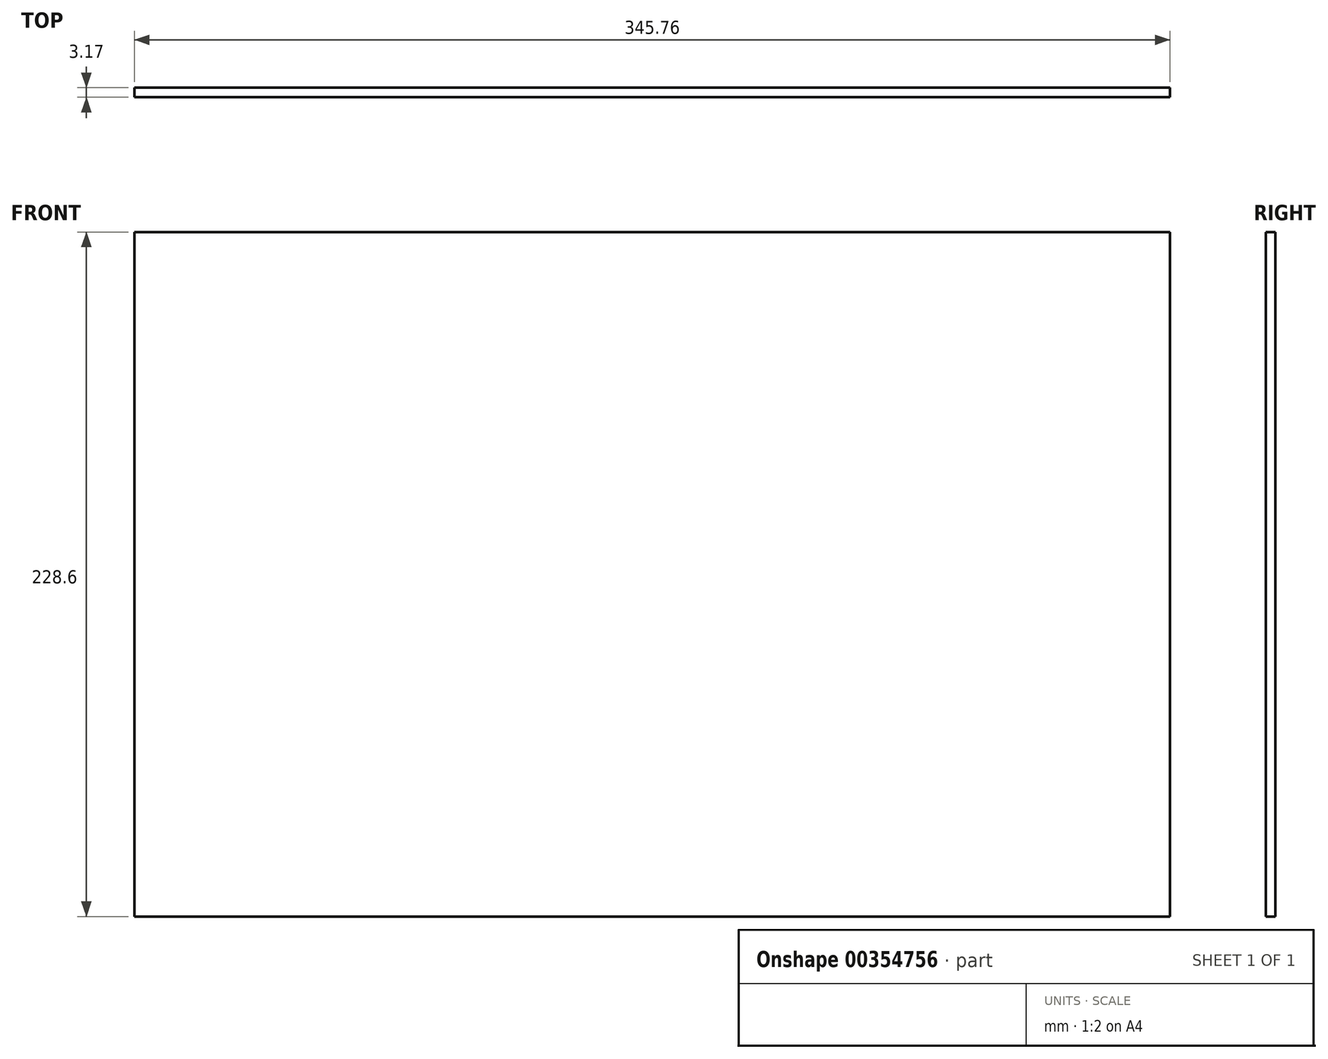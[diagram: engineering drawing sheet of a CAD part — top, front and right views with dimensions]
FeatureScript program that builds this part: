
annotation { "Feature Type Name" : "Feature", "Feature Type Description" : "" }
export const myFeature = defineFeature(function(context is Context, id is Id, definition is map)
    precondition{}
    {
        {
            var Q0;
            Q0=qCreatedBy(makeId("Front.planeOp"),FACE);
            var sketch = newSketch(context, id + "F0", { "sketchPlane" : qUnion([Q0])});
            skLineSegment(sketch, "E0.bottom", {"start": v(-172.88, 114.3) * mm, "end": v(172.88, 114.3) * mm});
            skLineSegment(sketch, "E0.top", {"start": v(-172.88, -114.3) * mm, "end": v(172.88, -114.3) * mm});
            skLineSegment(sketch, "E0.left", {"start": v(-172.88, 114.3) * mm, "end": v(-172.88, -114.3) * mm});
            skLineSegment(sketch, "E0.right", {"start": v(172.88, 114.3) * mm, "end": v(172.88, -114.3) * mm});
            skPoint(sketch, "E0.middle", {"position": v(0, 0) * mm});
            skSolve(sketch);
        }
        {
            var Q0;
            Q0 = qSketchRegion(id + "F0", true);
            extrude(context, id + "F1", {"entities" : qUnion([Q0]), "depth" : 3.17 * mm});
        }
    });
